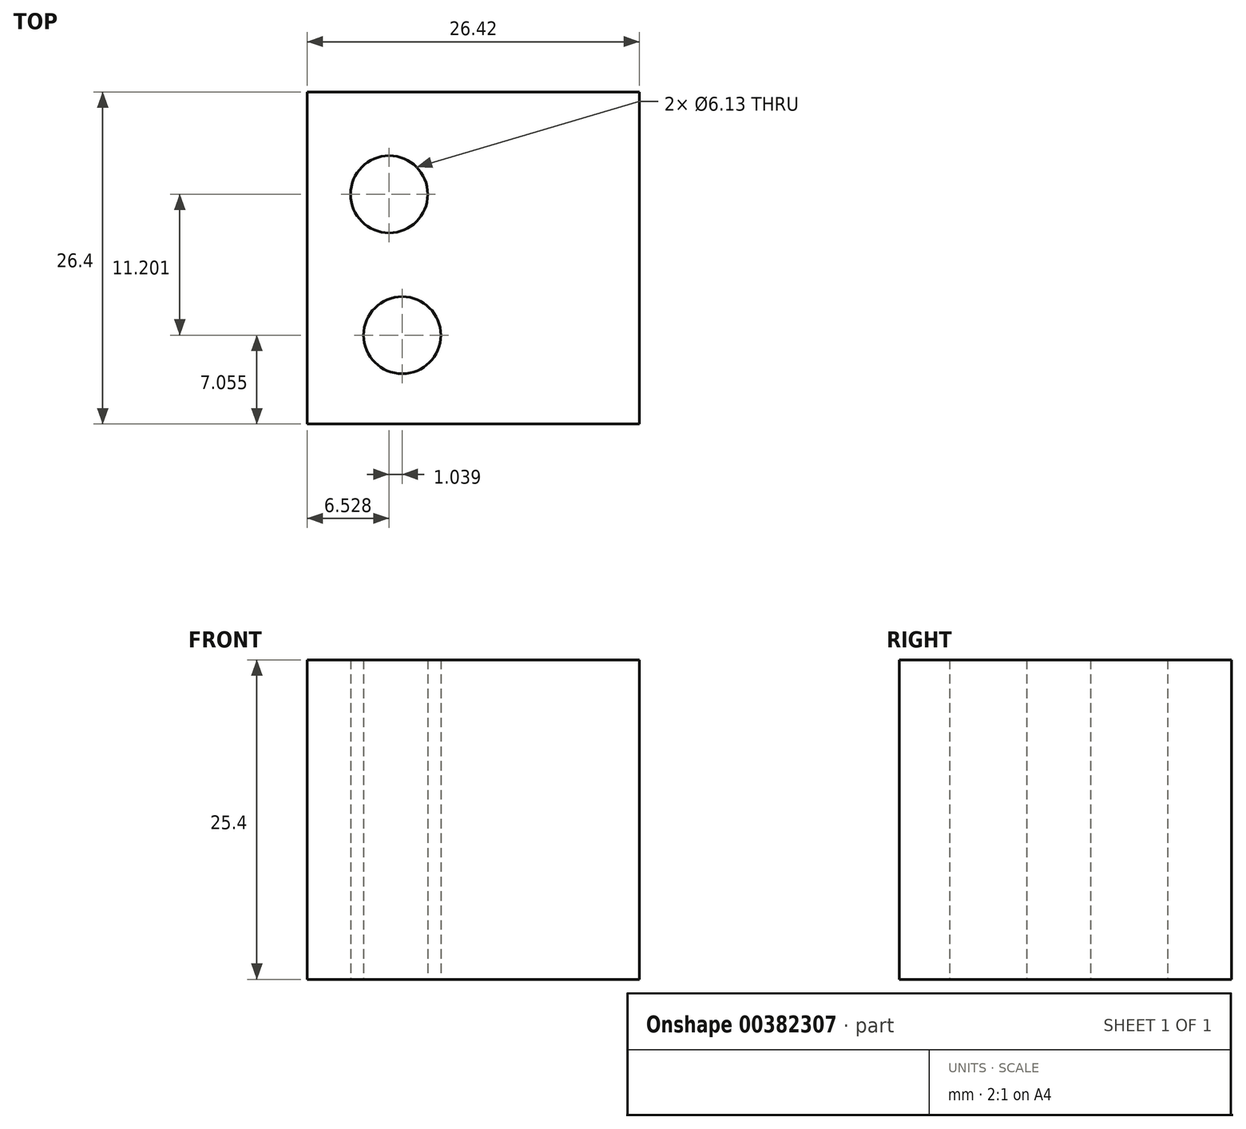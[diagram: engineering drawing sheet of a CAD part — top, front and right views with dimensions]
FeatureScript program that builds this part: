
annotation { "Feature Type Name" : "Feature", "Feature Type Description" : "" }
export const myFeature = defineFeature(function(context is Context, id is Id, definition is map)
    precondition{}
    {
        {
            var Q0;
            Q0=qCreatedBy(makeId("Top.planeOp"),FACE);
            var sketch = newSketch(context, id + "F0", { "sketchPlane" : qUnion([Q0])});
            skLineSegment(sketch, "E0.bottom", {"start": v(-93.54, 0) * mm, "end": v(-67.12, 0) * mm});
            skLineSegment(sketch, "E0.top", {"start": v(-93.54, -26.4) * mm, "end": v(-67.12, -26.4) * mm});
            skLineSegment(sketch, "E0.left", {"start": v(-93.54, 0) * mm, "end": v(-93.54, -26.4) * mm});
            skLineSegment(sketch, "E0.right", {"start": v(-67.12, 0) * mm, "end": v(-67.12, -26.4) * mm});
            skCircle(sketch, "E1", {"center": v(-85.97, -19.34) * mm, "radius": 3.07 * mm});
            skCircle(sketch, "E2", {"center": v(-87.01, -8.14) * mm, "radius": 3.07 * mm});
            skSolve(sketch);
        }
        {
            var Q0;
            Q0 = qSketchRegion(id + "F0", true);
            extrude(context, id + "F1", {"entities" : qUnion([Q0]), "depth" : 25.4 * mm});
        }
    });
